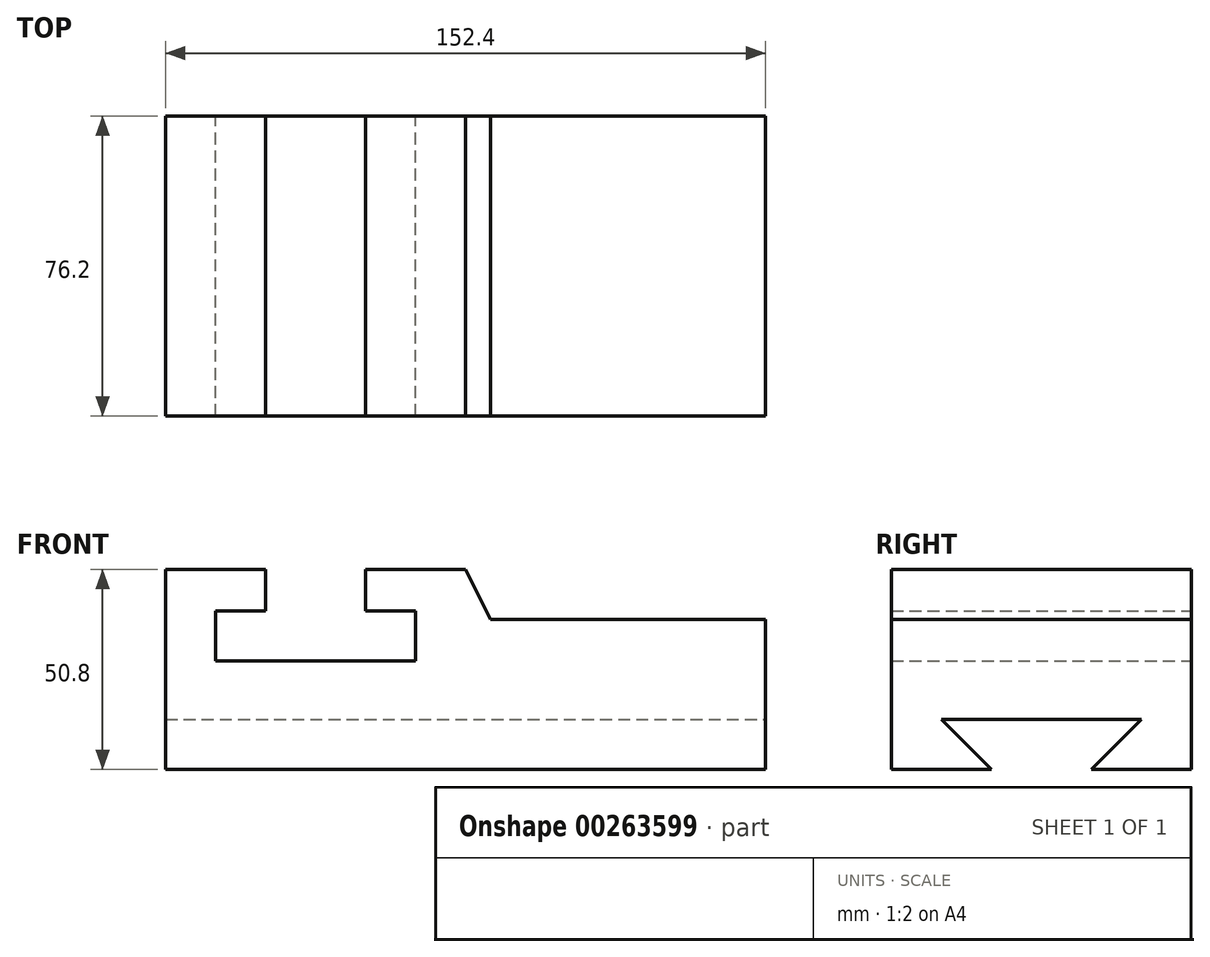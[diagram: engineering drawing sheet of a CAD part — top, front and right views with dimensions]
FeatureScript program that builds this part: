
annotation { "Feature Type Name" : "Feature", "Feature Type Description" : "" }
export const myFeature = defineFeature(function(context is Context, id is Id, definition is map)
    precondition{}
    {
        {
            var Q0;
            Q0=qCreatedBy(makeId("Front.planeOp"),FACE);
            var sketch = newSketch(context, id + "F0", { "sketchPlane" : qUnion([Q0])});
            skLineSegment(sketch, "E0.bottom", {"start": v(-74.54, 0) * mm, "end": v(77.86, 0) * mm});
            skLineSegment(sketch, "E0.left", {"start": v(-74.54, 0) * mm, "end": v(-74.54, 50.8) * mm});
            skLineSegment(sketch, "E1", {"start": v(77.86, 0) * mm, "end": v(77.86, 38.1) * mm});
            skLineSegment(sketch, "E2", {"start": v(8, 38.1) * mm, "end": v(77.86, 38.1) * mm});
            skLineSegment(sketch, "E3", {"start": v(1.66, 50.8) * mm, "end": v(8, 38.1) * mm});
            skLineSegment(sketch, "E4", {"start": v(-74.54, 50.8) * mm, "end": v(-49.14, 50.8) * mm});
            skLineSegment(sketch, "E5", {"start": v(1.66, 50.8) * mm, "end": v(-23.74, 50.8) * mm});
            skLineSegment(sketch, "E6", {"start": v(-49.14, 50.8) * mm, "end": v(-49.14, 40.33) * mm});
            skLineSegment(sketch, "E7", {"start": v(-23.74, 50.8) * mm, "end": v(-23.74, 40.33) * mm});
            skLineSegment(sketch, "E8", {"start": v(-23.74, 40.33) * mm, "end": v(-11.04, 40.33) * mm});
            skLineSegment(sketch, "E9", {"start": v(-49.14, 40.33) * mm, "end": v(-61.84, 40.33) * mm});
            skLineSegment(sketch, "E10", {"start": v(-61.84, 40.33) * mm, "end": v(-61.84, 27.63) * mm});
            skLineSegment(sketch, "E11", {"start": v(-11.04, 40.33) * mm, "end": v(-11.04, 27.63) * mm});
            skLineSegment(sketch, "E12", {"start": v(-11.04, 27.63) * mm, "end": v(-61.84, 27.63) * mm});
            skSolve(sketch);
        }
        {
            var Q0;
            Q0 = qSketchRegion(id + "F0", true);
            extrude(context, id + "F1", {"entities" : qUnion([Q0]), "depth" : 76.2 * mm});
        }
        {
            var Q0;
            Q0=makeQuery(id+"F1.opExtrude","SWEPT_FACE",FACE,{"disambiguationData":[OSD([sQuery(id+"F0.wireOp",EDGE,"E1")])]});
            var sketch = newSketch(context, id + "F2", { "sketchPlane" : qUnion([Q0])});
            skLineSegment(sketch, "E13", {"start": v(0, 0) * mm, "end": v(-25.4, 0) * mm});
            skLineSegment(sketch, "E14", {"start": v(-76.2, 0) * mm, "end": v(-50.8, 0) * mm});
            skLineSegment(sketch, "E15", {"start": v(-12.7, 12.7) * mm, "end": v(-63.5, 12.7) * mm});
            skLineSegment(sketch, "E16", {"start": v(-63.5, 12.7) * mm, "end": v(-50.8, 0) * mm});
            skLineSegment(sketch, "E17", {"start": v(-25.4, 0) * mm, "end": v(-12.7, 12.7) * mm});
            skSolve(sketch);
        }
        {
            var Q0;
            Q0=makeQuery(id+"F2.imprint","IMPRINT",FACE,{"disambiguationData":[TD([[makeQuery(id+"F2.imprint","IMPRINT",EDGE,{"derivedFrom":sQuery(id+"F2.wireOp",EDGE,"E15")}),1.0]])]});
            extrude(context, id + "F3", {"entities" : qUnion([Q0]), "operationType" : NewBodyOperationType.REMOVE, "oppositeDirection" : true, "depth" : 152.4 * mm});
        }
    });
